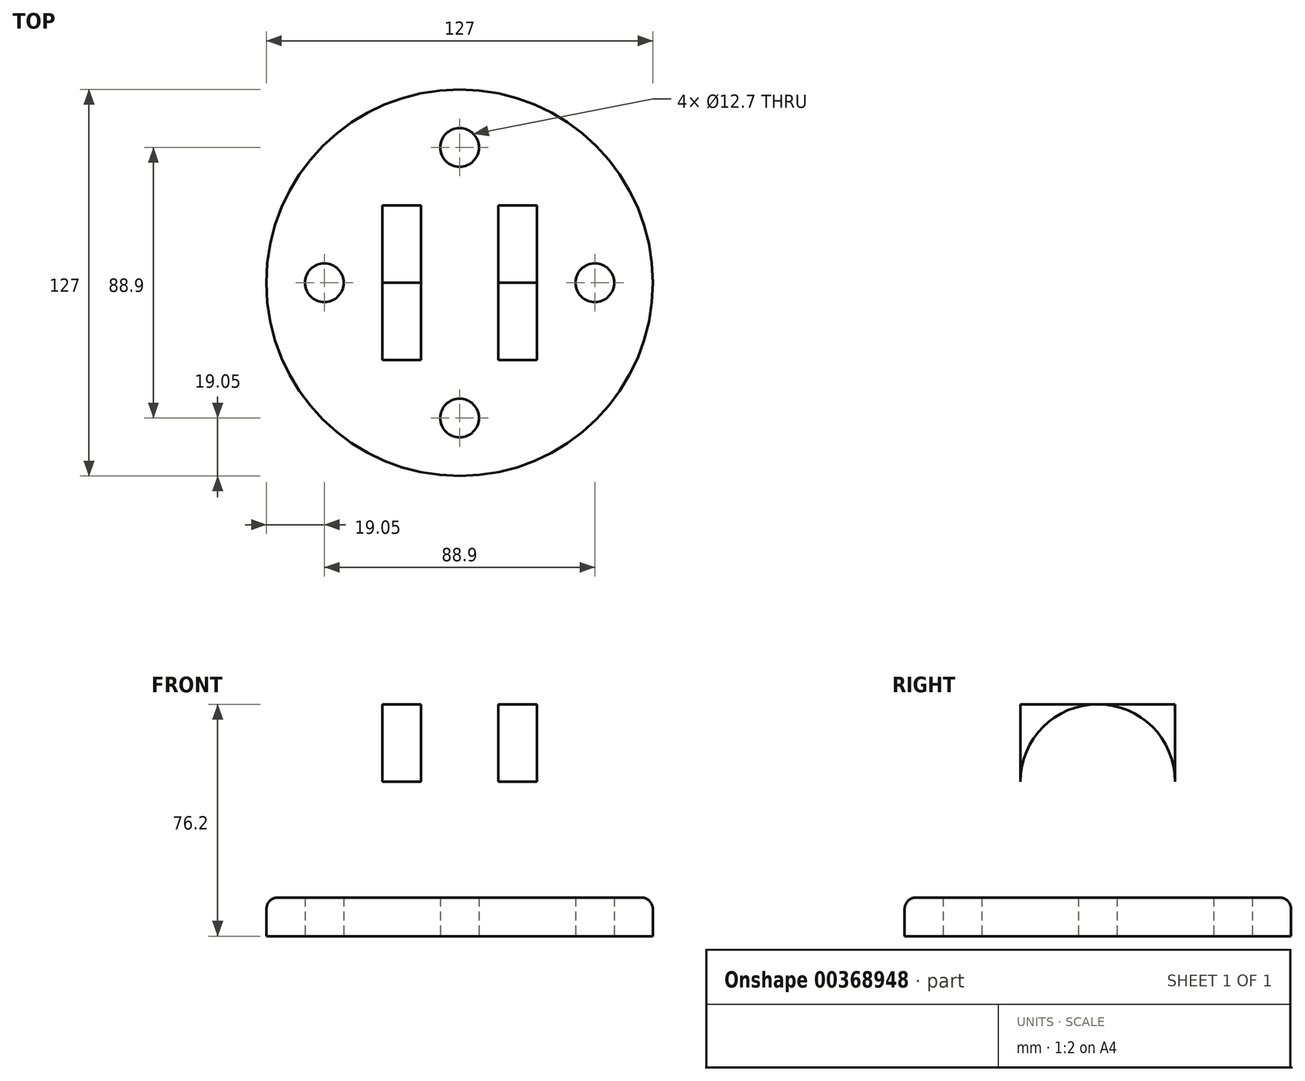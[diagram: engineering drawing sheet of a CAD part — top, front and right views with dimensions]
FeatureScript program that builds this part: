
annotation { "Feature Type Name" : "Feature", "Feature Type Description" : "" }
export const myFeature = defineFeature(function(context is Context, id is Id, definition is map)
    precondition{}
    {
        {
            var Q0;
            Q0=qCreatedBy(makeId("Top.planeOp"),FACE);
            var sketch = newSketch(context, id + "F0", { "sketchPlane" : qUnion([Q0])});
            skCircle(sketch, "E0", {"center": v(0, 0) * mm, "radius": 63.5 * mm});
            skCircle(sketch, "E1", {"center": v(0, 0) * mm, "radius": 44.45 * mm, "construction": true});
            skCircle(sketch, "E2", {"center": v(0, 44.45) * mm, "radius": 6.35 * mm});
            skCircle(sketch, "E3", {"center": v(0, -44.45) * mm, "radius": 6.35 * mm});
            skCircle(sketch, "E4", {"center": v(44.45, 0) * mm, "radius": 6.35 * mm});
            skCircle(sketch, "E5", {"center": v(-44.45, 0) * mm, "radius": 6.35 * mm});
            skSolve(sketch);
        }
        {
            var Q0;
            Q0 = qSketchRegion(id + "F0", true);
            extrude(context, id + "F1", {"entities" : qUnion([Q0]), "depth" : 12.7 * mm});
        }
        {
            var Q0;
            Q0=makeQuery(id+"F1.opExtrude","CAP_FACE",FACE,{"disambiguationData":[OSD([sQuery(id+"F0.wireOp",EDGE,"E0"),sQuery(id+"F0.wireOp",EDGE,"E2"),sQuery(id+"F0.wireOp",EDGE,"E3"),sQuery(id+"F0.wireOp",EDGE,"E4"),sQuery(id+"F0.wireOp",EDGE,"E5")])],"isStart":false});
            var sketch = newSketch(context, id + "F2", { "sketchPlane" : qUnion([Q0])});
            skLineSegment(sketch, "E6", {"start": v(-25.4, 25.4) * mm, "end": v(-25.4, -25.4) * mm});
            skLineSegment(sketch, "E7", {"start": v(-25.4, -25.4) * mm, "end": v(25.4, -25.4) * mm});
            skLineSegment(sketch, "E8", {"start": v(25.4, -25.4) * mm, "end": v(25.4, 25.4) * mm});
            skLineSegment(sketch, "E9", {"start": v(25.4, 25.4) * mm, "end": v(-25.4, 25.4) * mm});
            skLineSegment(sketch, "E10", {"start": v(-12.7, 25.4) * mm, "end": v(-12.7, -25.4) * mm});
            skLineSegment(sketch, "E11", {"start": v(12.7, 25.4) * mm, "end": v(12.7, -25.4) * mm});
            skSolve(sketch);
        }
        {
            var Q0;
            {var subQ0=sQuery(id+"F2.wireOp",EDGE,"E10");Q0=makeQuery(id+"F2.imprint","IMPRINT",FACE,{"disambiguationData":[TD([[makeQuery(id+"F2.imprint","IMPRINT",EDGE,{"derivedFrom":subQ0}),1.0]])]});}
            extrude(context, id + "F3", {"entities" : qUnion([Q0]), "operationType" : NewBodyOperationType.ADD, "depth" : 12.7 * mm});
        }
        {
            var Q0;
            {var subQ0=sQuery(id+"F2.wireOp",EDGE,"E6");Q0=makeQuery(id+"F2.imprint","IMPRINT",FACE,{"disambiguationData":[TD([[makeQuery(id+"F2.imprint","IMPRINT",EDGE,{"derivedFrom":subQ0}),1.0]])]});}
            var Q1;
            {var subQ0=sQuery(id+"F2.wireOp",EDGE,"E8");Q1=makeQuery(id+"F2.imprint","IMPRINT",FACE,{"disambiguationData":[TD([[makeQuery(id+"F2.imprint","IMPRINT",EDGE,{"derivedFrom":subQ0}),1.0]])]});}
            extrude(context, id + "F4", {"entities" : qUnion([Q0, Q1]), "operationType" : NewBodyOperationType.ADD, "depth" : 63.5 * mm});
        }
        {
            var Q0;
            Q0=makeQuery(id+"F4.opExtrude","SWEPT_FACE",FACE,{"disambiguationData":[OSD([sQuery(id+"F2.wireOp",EDGE,"E6")])]});
            var sketch = newSketch(context, id + "F5", { "sketchPlane" : qUnion([Q0])});
            skLineSegment(sketch, "E12", {"start": v(0, 76.2) * mm, "end": v(0, 50.8) * mm, "construction": true});
            skPoint(sketch, "E12.endSnap0", {"position": v(0, 76.2) * mm});
            skArc(sketch, "E13", {"start": v(-25.4, 50.8) * mm, "mid": v(0, 76.2) * mm, "end": v(25.4, 50.8) * mm});
            skCircle(sketch, "E14", {"center": v(0, 50.8) * mm, "radius": 9.53 * mm});
            skSolve(sketch);
        }
        {
            var Q0;
            Q0 = qSketchRegion(id + "F5", true);
            var Q1;
            {var subQ0=sQuery(id+"F5.wireOp",EDGE,"E13");var subQ1=sQuery(id+"F2.wireOp",EDGE,"E6");var subQ4=makeQuery(id+"F4.opExtrude","CAP_EDGE",EDGE,{"disambiguationData":[OSD([subQ1])],"isStart":false});var subQ5=makeQuery(id+"F5.imprint","INTERSECT",VERTEX,{"derivedFrom":[subQ4,subQ0]});Q1=makeQuery(id+"F5.imprint","IMPRINT",FACE,{"disambiguationData":[TD([[makeQuery(id+"F5.imprint","IMPRINT",EDGE,{"disambiguationData":[TD([[subQ5,1.0]])],"derivedFrom":subQ0}),1.0]])]});}
            var Q2;
            {var subQ0=sQuery(id+"F5.wireOp",EDGE,"E13");var subQ1=sQuery(id+"F2.wireOp",EDGE,"E6");var subQ4=makeQuery(id+"F4.opExtrude","CAP_EDGE",EDGE,{"disambiguationData":[OSD([subQ1])],"isStart":false});var subQ5=makeQuery(id+"F5.imprint","INTERSECT",VERTEX,{"derivedFrom":[subQ4,subQ0]});Q2=makeQuery(id+"F5.imprint","IMPRINT",FACE,{"disambiguationData":[TD([[makeQuery(id+"F5.imprint","IMPRINT",EDGE,{"disambiguationData":[TD([[subQ5,-1.0]])],"derivedFrom":subQ0}),1.0]])]});}
            extrude(context, id + "F6", {"entities" : qUnion([Q0, Q1, Q2]), "operationType" : NewBodyOperationType.REMOVE, "endBound" : BoundingType.THROUGH_ALL, "oppositeDirection" : true, "depth" : 25.4 * mm});
        }
        {
            var Q0;
            Q0=makeQuery(id+"F1.opExtrude","CAP_EDGE",EDGE,{"disambiguationData":[OSD([sQuery(id+"F0.wireOp",EDGE,"E0")])],"isStart":false});
            var Q1;
            Q1=makeQuery(id+"F4.opExtrude","CAP_EDGE",EDGE,{"disambiguationData":[OSD([sQuery(id+"F2.wireOp",EDGE,"E6")])],"isStart":true});
            var Q2;
            Q2=makeQuery(id+"F4.opExtrude","CAP_EDGE",EDGE,{"disambiguationData":[OSD([sQuery(id+"F2.wireOp",EDGE,"E8")])],"isStart":true});
            var Q3;
            {var subQ0=sQuery(id+"F2.wireOp",EDGE,"E7");Q3=makeQuery(id+"F4.boolean.opBoolean","MERGE",EDGE,{"derivedFrom":[makeQuery(id+"F3.opExtrude","CAP_EDGE",EDGE,{"disambiguationData":[OSD([subQ0])],"isStart":true}),makeQuery(id+"F4.opExtrude","CAP_EDGE",EDGE,{"disambiguationData":[OSD([subQ0]),TDD([makeQuery(id+"F2.imprint","IMPRINT",EDGE,{"disambiguationData":[TD([[makeQuery(id+"F2.imprint","INTERSECT",VERTEX,{"derivedFrom":[sQuery(id+"F2.wireOp",EDGE,"E6"),subQ0]}),-1.0]])],"derivedFrom":subQ0})])],"isStart":true}),makeQuery(id+"F4.opExtrude","CAP_EDGE",EDGE,{"disambiguationData":[OSD([subQ0]),TDD([makeQuery(id+"F2.imprint","IMPRINT",EDGE,{"disambiguationData":[TD([[makeQuery(id+"F2.imprint","INTERSECT",VERTEX,{"derivedFrom":[subQ0,sQuery(id+"F2.wireOp",EDGE,"E8")]}),1.0]])],"derivedFrom":subQ0})])],"isStart":true})]});}
            var Q4;
            {var subQ0=sQuery(id+"F2.wireOp",EDGE,"E9");Q4=makeQuery(id+"F4.boolean.opBoolean","MERGE",EDGE,{"derivedFrom":[makeQuery(id+"F3.opExtrude","CAP_EDGE",EDGE,{"disambiguationData":[OSD([subQ0])],"isStart":true}),makeQuery(id+"F4.opExtrude","CAP_EDGE",EDGE,{"disambiguationData":[OSD([subQ0]),TDD([makeQuery(id+"F2.imprint","IMPRINT",EDGE,{"disambiguationData":[TD([[makeQuery(id+"F2.imprint","INTERSECT",VERTEX,{"derivedFrom":[sQuery(id+"F2.wireOp",EDGE,"E8"),subQ0]}),-1.0]])],"derivedFrom":subQ0})])],"isStart":true}),makeQuery(id+"F4.opExtrude","CAP_EDGE",EDGE,{"disambiguationData":[OSD([subQ0]),TDD([makeQuery(id+"F2.imprint","IMPRINT",EDGE,{"disambiguationData":[TD([[makeQuery(id+"F2.imprint","INTERSECT",VERTEX,{"derivedFrom":[sQuery(id+"F2.wireOp",EDGE,"E6"),subQ0]}),1.0]])],"derivedFrom":subQ0})])],"isStart":true})]});}
            fillet(context, id + "F7", {"entities" : qUnion([Q0, Q1, Q2, Q3, Q4]), "radius" : 3.8 * mm, "tangentPropagation" : true, "allowEdgeOverflow" : false});
        }
    });
